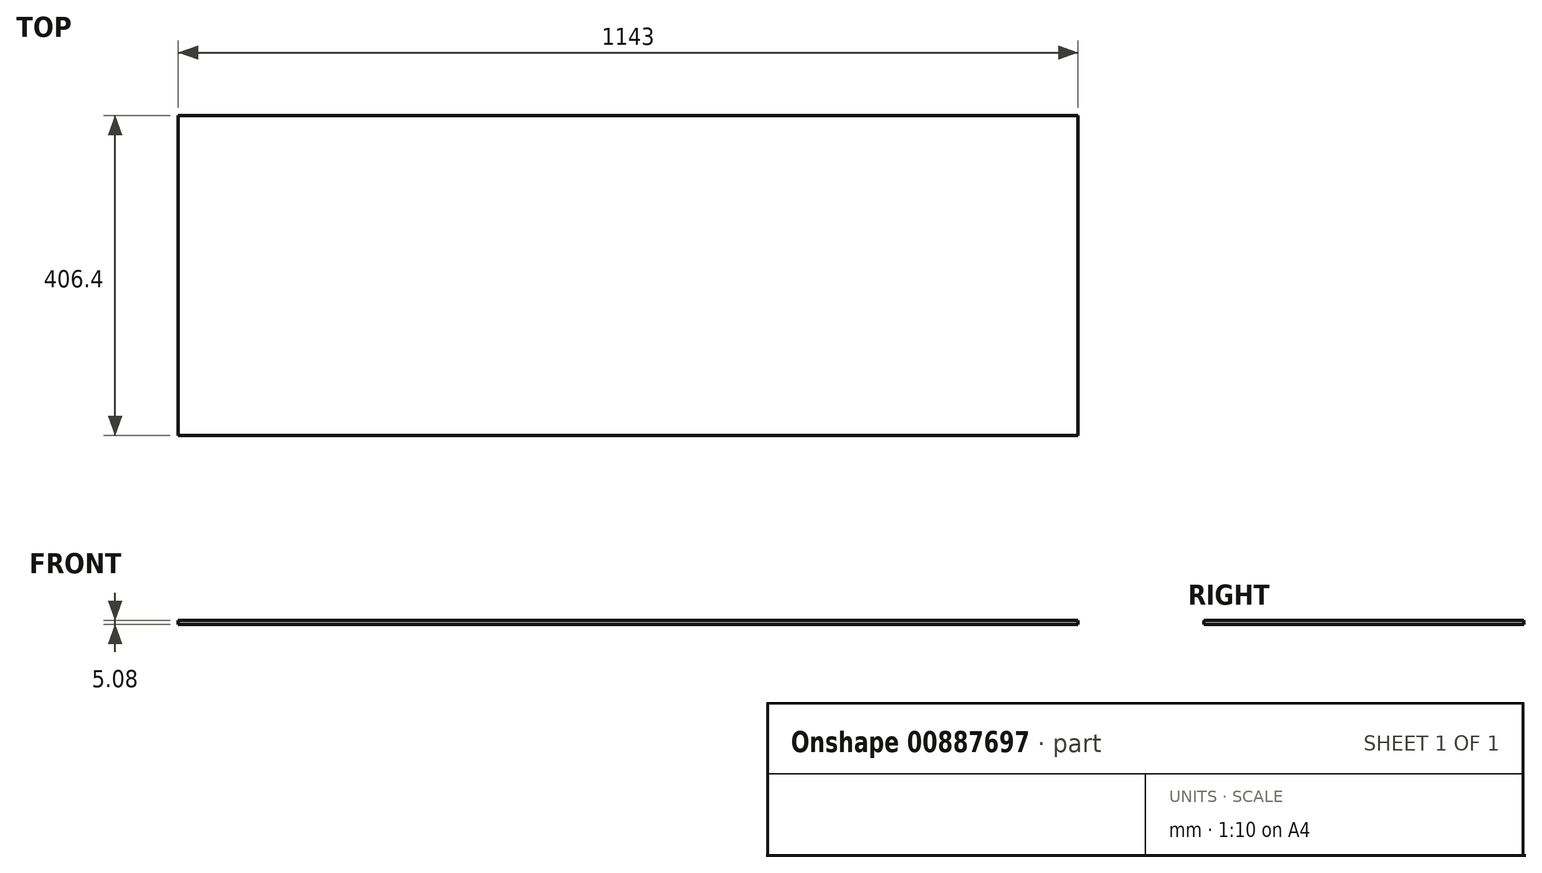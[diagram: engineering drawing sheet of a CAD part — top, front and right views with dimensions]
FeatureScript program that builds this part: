
annotation { "Feature Type Name" : "Feature", "Feature Type Description" : "" }
export const myFeature = defineFeature(function(context is Context, id is Id, definition is map)
    precondition{}
    {
        {
            var Q0;
            Q0=qCreatedBy(makeId("Top.planeOp"),FACE);
            var sketch = newSketch(context, id + "F0", { "sketchPlane" : qUnion([Q0])});
            skLineSegment(sketch, "E0.bottom", {"start": v(-571.5, 203.2) * mm, "end": v(571.5, 203.2) * mm});
            skLineSegment(sketch, "E0.top", {"start": v(-571.5, -203.2) * mm, "end": v(571.5, -203.2) * mm});
            skLineSegment(sketch, "E0.left", {"start": v(-571.5, 203.2) * mm, "end": v(-571.5, -203.2) * mm});
            skLineSegment(sketch, "E0.right", {"start": v(571.5, 203.2) * mm, "end": v(571.5, -203.2) * mm});
            skPoint(sketch, "E0.middle", {"position": v(0, 0) * mm});
            skSolve(sketch);
        }
        {
            var Q0;
            Q0=makeQuery(id+"F0.imprint","IMPRINT",FACE,{"disambiguationData":[TD([[makeQuery(id+"F0.imprint","IMPRINT",EDGE,{"derivedFrom":sQuery(id+"F0.wireOp",EDGE,"E0.bottom")}),-1.0]])]});
            extrude(context, id + "F1", {"entities" : qUnion([Q0]), "depth" : 5.08 * mm, "offsetDistance" : 25.4 * mm});
        }
    });
